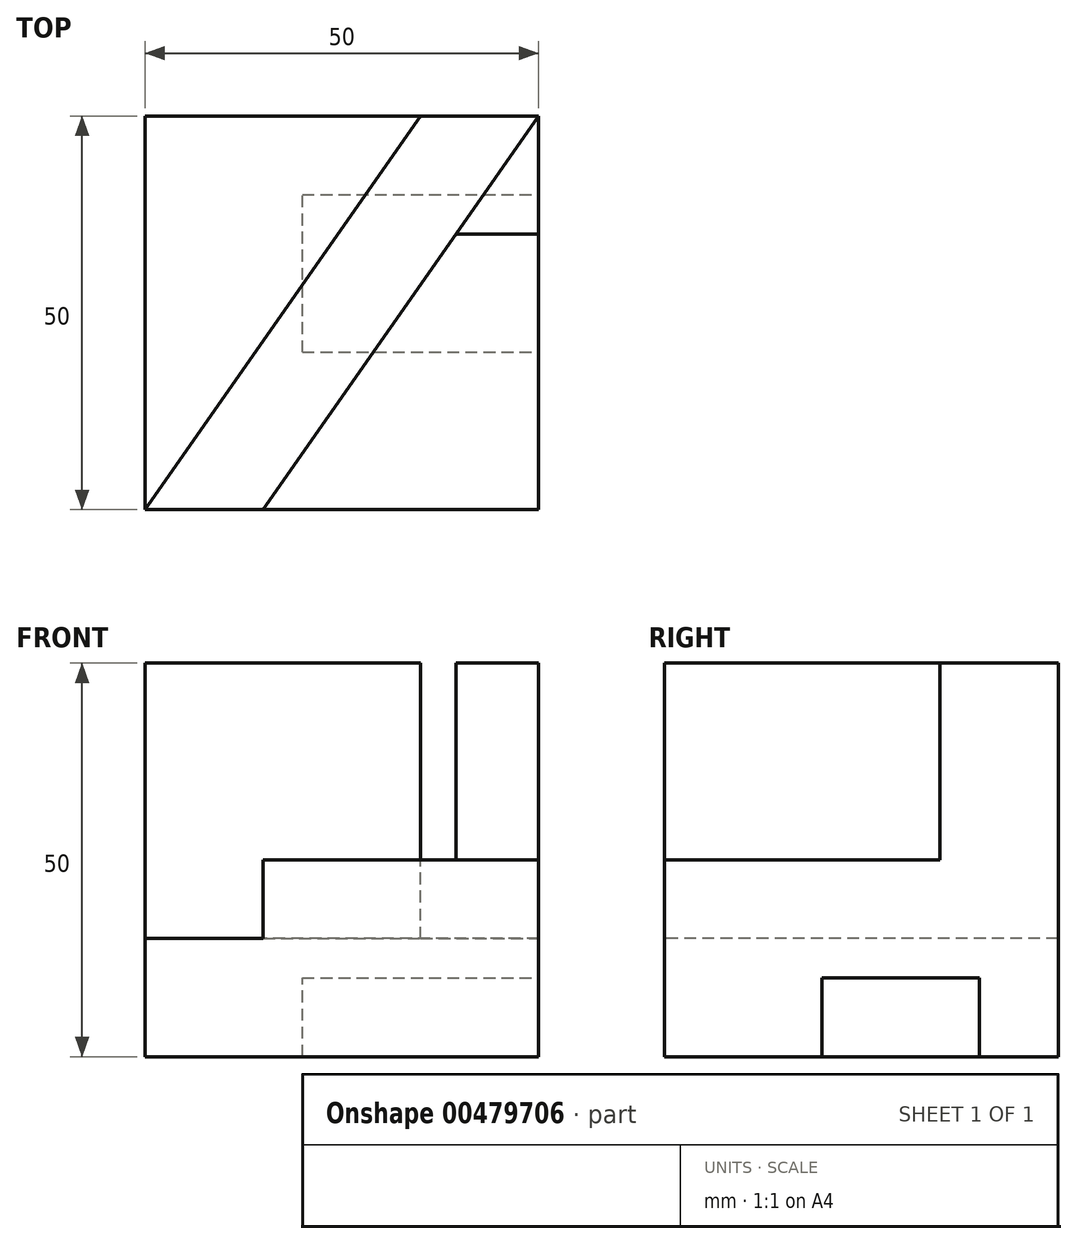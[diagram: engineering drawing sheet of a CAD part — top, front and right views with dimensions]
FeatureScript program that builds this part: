
annotation { "Feature Type Name" : "Feature", "Feature Type Description" : "" }
export const myFeature = defineFeature(function(context is Context, id is Id, definition is map)
    precondition{}
    {
        {
            var Q0;
            Q0=qCreatedBy(makeId("Top.planeOp"),FACE);
            var sketch = newSketch(context, id + "F0", { "sketchPlane" : qUnion([Q0])});
            skLineSegment(sketch, "E0.bottom", {"start": v(0, 0) * mm, "end": v(50, 0) * mm});
            skLineSegment(sketch, "E0.top", {"start": v(0, 50) * mm, "end": v(50, 50) * mm});
            skLineSegment(sketch, "E0.left", {"start": v(0, 0) * mm, "end": v(0, 50) * mm});
            skLineSegment(sketch, "E0.right", {"start": v(50, 0) * mm, "end": v(50, 50) * mm});
            skSolve(sketch);
        }
        {
            var Q0;
            Q0=qSketchRegion(id+"F0",true);
            extrude(context, id + "F1", {"entities" : qUnion([Q0]), "depth" : 50 * mm});
        }
        {
            var Q0;
            Q0=makeQuery(id+"F1.opExtrude","CAP_FACE",FACE,{"disambiguationData":[OSD([sQuery(id+"F0.wireOp",EDGE,"E0.bottom"),sQuery(id+"F0.wireOp",EDGE,"E0.top"),sQuery(id+"F0.wireOp",EDGE,"E0.left"),sQuery(id+"F0.wireOp",EDGE,"E0.right")])],"isStart":false});
            var sketch = newSketch(context, id + "F2", { "sketchPlane" : qUnion([Q0])});
            skLineSegment(sketch, "E1", {"start": v(50, 50) * mm, "end": v(15, 0) * mm});
            skLineSegment(sketch, "E2", {"start": v(0, 0) * mm, "end": v(35, 50) * mm});
            skSolve(sketch);
        }
        {
            var Q0;
            Q0=qSketchRegion(id+"F2",true);
            var Q1;
            {var subQ0=sQuery(id+"F2.wireOp",EDGE,"E1");Q1=makeQuery(id+"F2.imprint","IMPRINT",FACE,{"disambiguationData":[TD([[makeQuery(id+"F2.imprint","IMPRINT",EDGE,{"derivedFrom":subQ0}),-1.0]])]});}
            extrude(context, id + "F3", {"entities" : qUnion([Q0, Q1]), "operationType" : NewBodyOperationType.REMOVE, "oppositeDirection" : true, "depth" : 35 * mm});
        }
        {
            var Q0;
            Q0=makeQuery(id+"F1.opExtrude","SWEPT_FACE",FACE,{"disambiguationData":[OSD([sQuery(id+"F0.wireOp",EDGE,"E0.right")])]});
            var sketch = newSketch(context, id + "F4", { "sketchPlane" : qUnion([Q0])});
            skLineSegment(sketch, "E3.bottom", {"start": v(20, 0) * mm, "end": v(40, 0) * mm});
            skLineSegment(sketch, "E3.top", {"start": v(20, 10) * mm, "end": v(40, 10) * mm});
            skLineSegment(sketch, "E3.left", {"start": v(20, 0) * mm, "end": v(20, 10) * mm});
            skLineSegment(sketch, "E3.right", {"start": v(40, 0) * mm, "end": v(40, 10) * mm});
            skSolve(sketch);
        }
        {
            var Q0;
            Q0=qSketchRegion(id+"F4",true);
            extrude(context, id + "F5", {"entities" : qUnion([Q0]), "operationType" : NewBodyOperationType.REMOVE, "oppositeDirection" : true, "depth" : 30 * mm});
        }
        {
            var Q0;
            {var subQ0=sQuery(id+"F0.wireOp",EDGE,"E0.bottom");var subQ1=sQuery(id+"F0.wireOp",EDGE,"E0.right");Q0=makeQuery(id+"F3.boolean.opBoolean","SPLIT",FACE,{"disambiguationData":[TD([makeQuery(id+"F1.opExtrude","SWEPT_FACE",FACE,{"disambiguationData":[OSD([subQ0])]})])],"derivedFrom":makeQuery(id+"F1.opExtrude","CAP_FACE",FACE,{"disambiguationData":[OSD([subQ0,sQuery(id+"F0.wireOp",EDGE,"E0.top"),sQuery(id+"F0.wireOp",EDGE,"E0.left"),subQ1])],"isStart":false})});}
            var sketch = newSketch(context, id + "F6", { "sketchPlane" : qUnion([Q0])});
            skLineSegment(sketch, "E4", {"start": v(39.5, 35) * mm, "end": v(50, 35) * mm});
            skLineSegment(sketch, "E5", {"start": v(50, 35) * mm, "end": v(50, 0) * mm});
            skLineSegment(sketch, "E6", {"start": v(50, 0) * mm, "end": v(15, 0) * mm});
            skLineSegment(sketch, "E7", {"start": v(15, 0) * mm, "end": v(39.5, 35) * mm});
            skSolve(sketch);
        }
        {
            var Q0;
            Q0=qSketchRegion(id+"F6",true);
            extrude(context, id + "F7", {"entities" : qUnion([Q0]), "operationType" : NewBodyOperationType.REMOVE, "oppositeDirection" : true, "depth" : 25 * mm});
        }
    });
